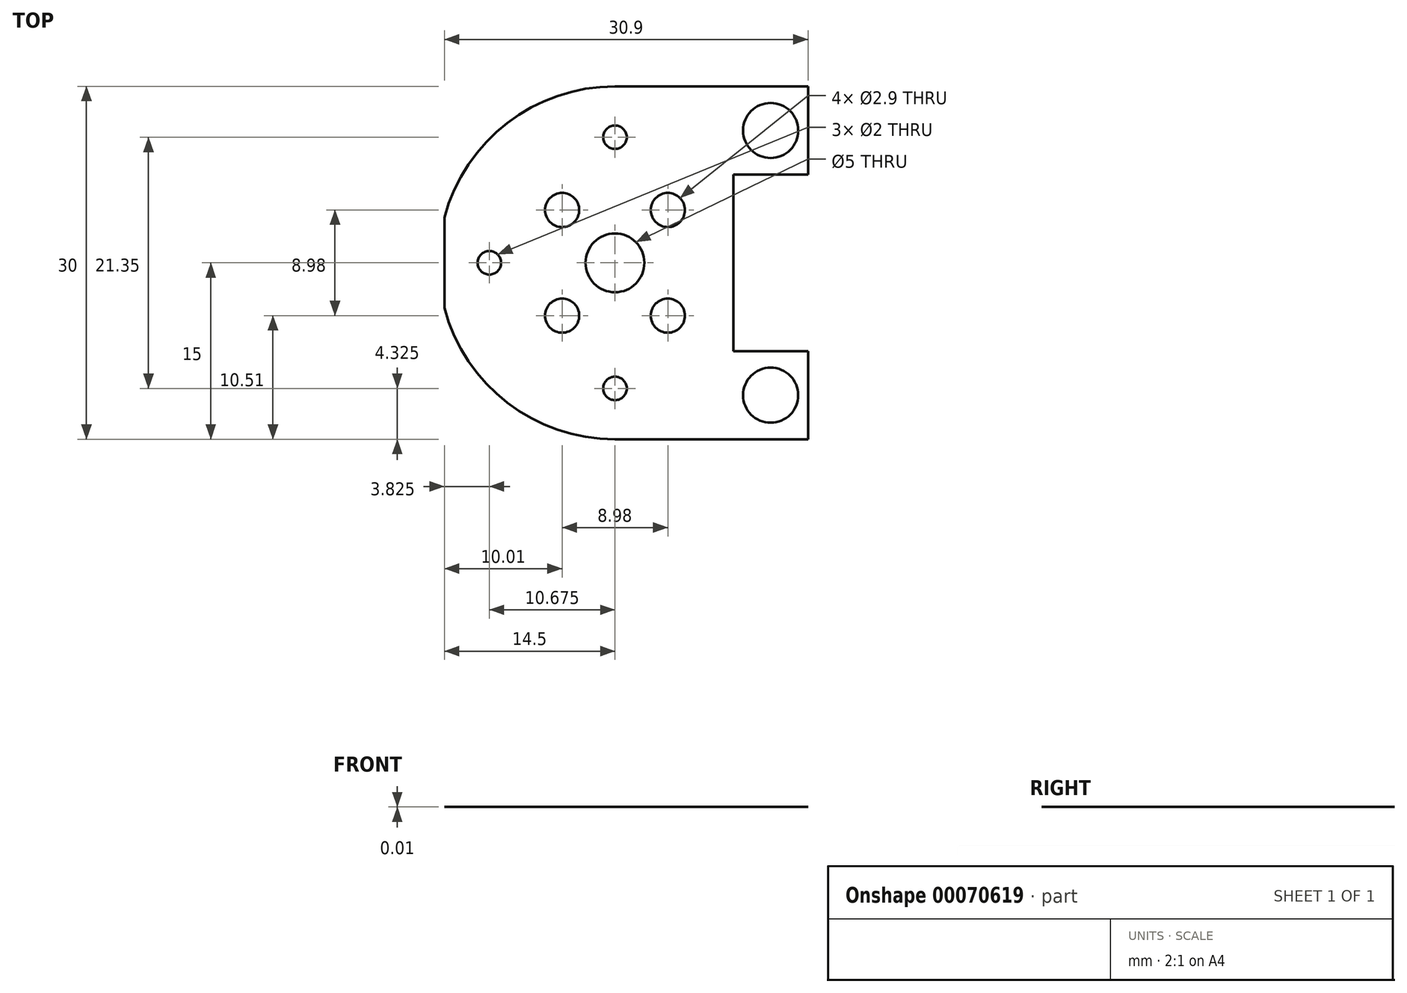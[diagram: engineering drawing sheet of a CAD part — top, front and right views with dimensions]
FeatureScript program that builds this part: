
annotation { "Feature Type Name" : "Feature", "Feature Type Description" : "" }
export const myFeature = defineFeature(function(context is Context, id is Id, definition is map)
    precondition{}
    {
        {
            var Q0;
            Q0=qCreatedBy(makeId("Top.planeOp"),FACE);
            var sketch = newSketch(context, id + "F0", { "sketchPlane" : qUnion([Q0])});
            skCircle(sketch, "E0", {"center": v(0, 0) * mm, "radius": 2.5 * mm});
            skLineSegment(sketch, "E1.bottom", {"start": v(0, 15) * mm, "end": v(16.4, 15) * mm});
            skLineSegment(sketch, "E1.top", {"start": v(0, -15) * mm, "end": v(16.4, -15) * mm});
            skLineSegment(sketch, "E1.left", {"start": v(0, 15) * mm, "end": v(0, -15) * mm});
            skLineSegment(sketch, "E1.right", {"start": v(16.4, 15) * mm, "end": v(16.4, -15) * mm});
            skLineSegment(sketch, "E2.bottom", {"start": v(10.05, 7.5) * mm, "end": v(16.4, 7.5) * mm});
            skLineSegment(sketch, "E2.top", {"start": v(10.05, -7.5) * mm, "end": v(16.4, -7.5) * mm});
            skLineSegment(sketch, "E2.left", {"start": v(10.05, 7.5) * mm, "end": v(10.05, -7.5) * mm});
            skLineSegment(sketch, "E2.right", {"start": v(16.4, 7.5) * mm, "end": v(16.4, -7.5) * mm});
            skPoint(sketch, "E3.positionSnap0", {"position": v(10.05, 0) * mm});
            skArc(sketch, "E4", {"start": v(0, 15) * mm, "mid": v(-15, 0) * mm, "end": v(0, -15) * mm});
            skPoint(sketch, "E5", {"position": v(13.22, 11.25) * mm});
            skPoint(sketch, "E6.MirrorP", {"position": v(13.22, -11.25) * mm});
            skArc(sketch, "E7", {"start": v(-6.35, 0) * mm, "mid": v(-4.5, 4.5) * mm, "end": v(0, 6.35) * mm});
            skPoint(sketch, "E8", {"position": v(-4.5, 4.5) * mm});
            skPoint(sketch, "E9.1.0", {"position": v(-4.5, -4.5) * mm});
            skPoint(sketch, "E9.2.0", {"position": v(4.5, -4.5) * mm});
            skPoint(sketch, "E9.3.0", {"position": v(4.5, 4.5) * mm});
            skPoint(sketch, "E10", {"position": v(0, 10.67) * mm});
            skPoint(sketch, "E11", {"position": v(-10.67, 0) * mm});
            skPoint(sketch, "E12.MirrorP", {"position": v(0, -10.67) * mm});
            skLineSegment(sketch, "E13", {"start": v(-14.5, 8.24) * mm, "end": v(-14.5, -8.02) * mm});
            skPoint(sketch, "E14", {"position": v(-15, 0) * mm});
            skSolve(sketch);
        }
        {
            var Q0;
            Q0=makeQuery(id+"F0.imprint","IMPRINT",FACE,{"disambiguationData":[TD([[makeQuery(id+"F0.imprint","IMPRINT",EDGE,{"derivedFrom":sQuery(id+"F0.wireOp",EDGE,"E0")}),-1.0]])]});
            var Q1;
            {var subQ2=sQuery(id+"F0.wireOp",EDGE,"E1.bottom");Q1=makeQuery(id+"F0.imprint","IMPRINT",FACE,{"disambiguationData":[TD([[makeQuery(id+"F0.imprint","IMPRINT",EDGE,{"derivedFrom":subQ2}),-1.0]])]});}
            extrude(context, id + "F1", {"entities" : qUnion([Q0, Q1]), "depth" : 1 / 101.6 * mm});
        }
        {
            var Q0;
            Q0=sQuery(id+"F0.wireOp",VERTEX,"E5");
            var Q1;
            Q1=sQuery(id+"F0.wireOp",VERTEX,"E6.MirrorP");
            var Q2;
            Q2=makeQuery(id+"F1.opExtrude","SWEPT_BODY",BODY,{"disambiguationData":[OSD([sQuery(id+"F0.wireOp",EDGE,"E0"),sQuery(id+"F0.wireOp",EDGE,"841147f9-053d-461c-8abe-5e9fd89ba898.1.0"),sQuery(id+"F0.wireOp",EDGE,"E1.bottom"),sQuery(id+"F0.wireOp",EDGE,"E1.top"),sQuery(id+"F0.wireOp",EDGE,"E1.right"),sQuery(id+"F0.wireOp",EDGE,"225ec38d-f954-42cf-a89d-ad5c54df0c93.1.0"),sQuery(id+"F0.wireOp",EDGE,"225ec38d-f954-42cf-a89d-ad5c54df0c93.2.0"),sQuery(id+"F0.wireOp",EDGE,"225ec38d-f954-42cf-a89d-ad5c54df0c93.3.0"),sQuery(id+"F0.wireOp",EDGE,"E2.bottom"),sQuery(id+"F0.wireOp",EDGE,"E2.top"),sQuery(id+"F0.wireOp",EDGE,"E2.left"),sQuery(id+"F0.wireOp",EDGE,"E4")])]});
            hole(context, id + "F2", {"style" : HoleStyle.C_SINK, "endStyle" : HoleEndStyle.THROUGH, "oppositeDirection" : true, "holeDiameter" : 2.5 * mm, "cSinkDiameter" : 4.7 * mm, "cSinkAngle" : 90 * degree, "locations" : qUnion([Q0, Q1]), "scope" : qUnion([Q2]), "isTappedThrough" : true});
        }
        {
            var Q0;
            Q0=sQuery(id+"F0.wireOp",VERTEX,"E8");
            var Q1;
            Q1=sQuery(id+"F0.wireOp",VERTEX,"E9.3.0");
            var Q2;
            Q2=sQuery(id+"F0.wireOp",VERTEX,"E9.2.0");
            var Q3;
            Q3=sQuery(id+"F0.wireOp",VERTEX,"E9.1.0");
            var Q4;
            Q4=makeQuery(id+"F1.opExtrude","SWEPT_BODY",BODY,{"disambiguationData":[OSD([sQuery(id+"F0.wireOp",EDGE,"E0"),sQuery(id+"F0.wireOp",EDGE,"E1.bottom"),sQuery(id+"F0.wireOp",EDGE,"E1.top"),sQuery(id+"F0.wireOp",EDGE,"E1.right"),sQuery(id+"F0.wireOp",EDGE,"E2.bottom"),sQuery(id+"F0.wireOp",EDGE,"E2.top"),sQuery(id+"F0.wireOp",EDGE,"E2.left"),sQuery(id+"F0.wireOp",EDGE,"E4")])]});
            hole(context, id + "F3", {"style" : HoleStyle.SIMPLE, "endStyle" : HoleEndStyle.THROUGH, "oppositeDirection" : true, "holeDiameter" : 2.9 * mm, "locations" : qUnion([Q0, Q1, Q2, Q3]), "scope" : qUnion([Q4]), "isTappedThrough" : true});
        }
        {
            var Q0;
            Q0=sQuery(id+"F0.wireOp",VERTEX,"E10");
            var Q1;
            Q1=sQuery(id+"F0.wireOp",VERTEX,"E11");
            var Q2;
            Q2=sQuery(id+"F0.wireOp",VERTEX,"E12.MirrorP");
            var Q3;
            Q3=makeQuery(id+"F1.opExtrude","SWEPT_BODY",BODY,{"disambiguationData":[OSD([sQuery(id+"F0.wireOp",EDGE,"E0"),sQuery(id+"F0.wireOp",EDGE,"E1.bottom"),sQuery(id+"F0.wireOp",EDGE,"E1.top"),sQuery(id+"F0.wireOp",EDGE,"E1.right"),sQuery(id+"F0.wireOp",EDGE,"E2.bottom"),sQuery(id+"F0.wireOp",EDGE,"E2.top"),sQuery(id+"F0.wireOp",EDGE,"E2.left"),sQuery(id+"F0.wireOp",EDGE,"E4")])]});
            hole(context, id + "F4", {"style" : HoleStyle.SIMPLE, "endStyle" : HoleEndStyle.THROUGH, "oppositeDirection" : true, "holeDiameter" : 2 * mm, "locations" : qUnion([Q0, Q1, Q2]), "scope" : qUnion([Q3]), "isTappedThrough" : true});
        }
        {
            var Q0;
            Q0=makeQuery(id+"F1.opExtrude","SWEPT_FACE",FACE,{"disambiguationData":[OSD([sQuery(id+"F0.wireOp",EDGE,"E2.left")])]});
            var sketch = newSketch(context, id + "F5", { "sketchPlane" : qUnion([Q0])});
            skPoint(sketch, "E15", {"position": v(0, 3.18) * mm});
            skSolve(sketch);
        }
        {
            var Q0;
            Q0=sQuery(id+"F5.wireOp",VERTEX,"E15");
            var Q1;
            Q1=makeQuery(id+"F1.opExtrude","SWEPT_BODY",BODY,{"disambiguationData":[OSD([sQuery(id+"F0.wireOp",EDGE,"E0"),sQuery(id+"F0.wireOp",EDGE,"E1.bottom"),sQuery(id+"F0.wireOp",EDGE,"E1.top"),sQuery(id+"F0.wireOp",EDGE,"E1.right"),sQuery(id+"F0.wireOp",EDGE,"E2.bottom"),sQuery(id+"F0.wireOp",EDGE,"E2.top"),sQuery(id+"F0.wireOp",EDGE,"E2.left"),sQuery(id+"F0.wireOp",EDGE,"E4")])]});
            hole(context, id + "F6", {"style" : HoleStyle.SIMPLE, "endStyle" : HoleEndStyle.BLIND, "holeDiameter" : 2.05 * mm, "holeDepth" : 8 * mm, "locations" : qUnion([Q0]), "scope" : qUnion([Q1])});
        }
    });
